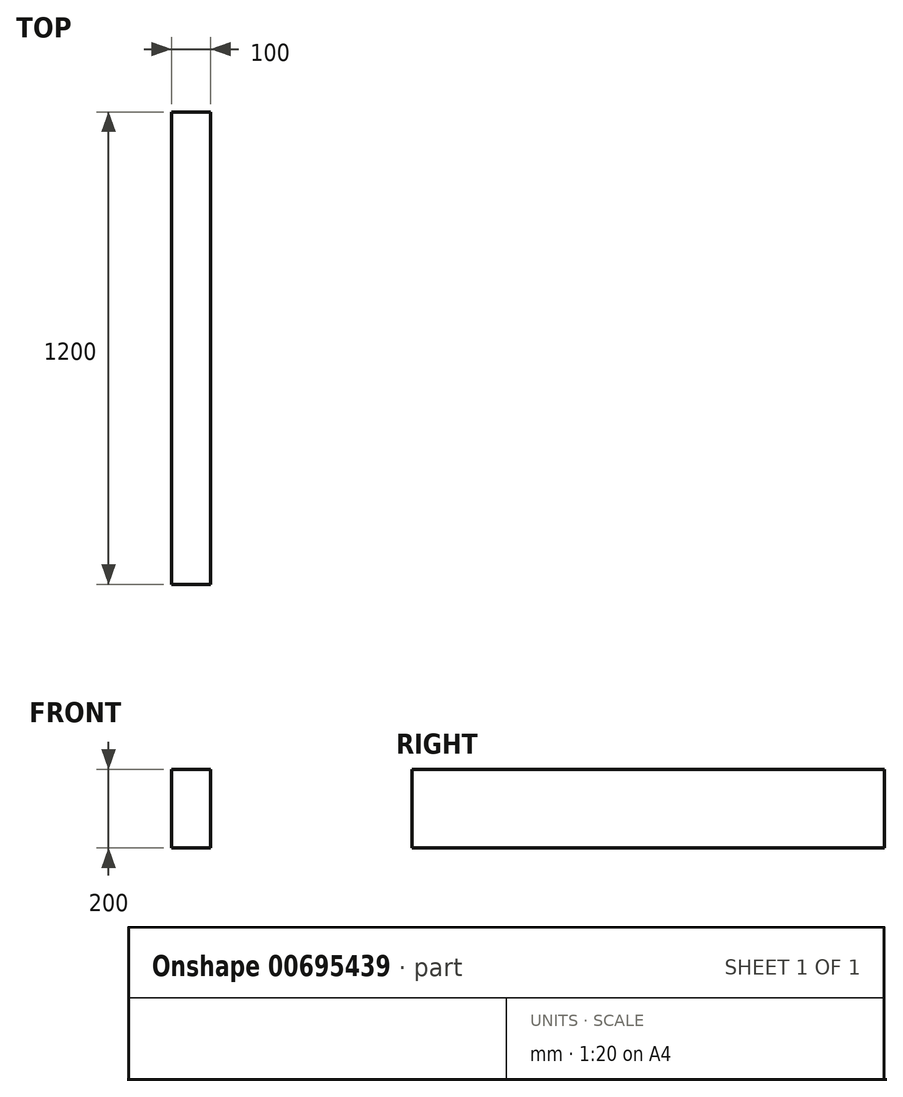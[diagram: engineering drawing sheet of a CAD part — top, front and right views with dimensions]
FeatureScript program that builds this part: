
annotation { "Feature Type Name" : "Feature", "Feature Type Description" : "" }
export const myFeature = defineFeature(function(context is Context, id is Id, definition is map)
    precondition{}
    {
        {
            var Q0;
            Q0=qCreatedBy(makeId("Front.planeOp"),FACE);
            var sketch = newSketch(context, id + "F0", { "sketchPlane" : qUnion([Q0])});
            skLineSegment(sketch, "E0.bottom", {"start": v(0, 0) * mm, "end": v(-100, 0) * mm});
            skLineSegment(sketch, "E0.top", {"start": v(0, 200) * mm, "end": v(-100, 200) * mm});
            skLineSegment(sketch, "E0.left", {"start": v(0, 0) * mm, "end": v(0, 200) * mm});
            skLineSegment(sketch, "E0.right", {"start": v(-100, 0) * mm, "end": v(-100, 200) * mm});
            skSolve(sketch);
        }
        {
            var Q0;
            Q0 = qSketchRegion(id + "F0", true);
            extrude(context, id + "F1", {"entities" : qUnion([Q0]), "depth" : 1200 * mm, "offsetDistance" : 25 * mm});
        }
    });
